SOLIDWORKS PART (.sldprt)
format: sldprt  version: not decoded by parser v0  size: 86,016 bytes
history: native  units: mm
features: sketch x4, plane x3, cut_extrude x3, material x1, extrude x1 (+13 scaffold rows collapsed)
feature tree (25):
  scaffold x13  (default folders/planes/origin — collapsed)
  material  "材质 <未指定>"
  plane  "前视基准面"
  plane  "上视基准面"
  plane  "右视基准面"
  sketch  "草图2"  dims[D1=2.5mm D2=0.5mm D3=1.5mm]
  extrude  "凸台-拉伸1"  Depth=1.5mm
  sketch  "草图3"  dims[D1=~0.141057mm]
  cut_extrude  "切除-拉伸1"  Depth=1.5mm
  sketch  "草图4"  dims[D1=~0.193892mm]
  cut_extrude  "切除-拉伸2"  Depth=0.5mm
  sketch  "草图5"  dims[D1=~0.309787mm]
  cut_extrude  "切除-拉伸3"  Depth=0.2mm
decode coverage: 8 of 8 modeling features carry decoded parameters
note: ~ marks probable driven/reference dimensions
note: suppression state not decoded; provenance and decode notes live in map.json
